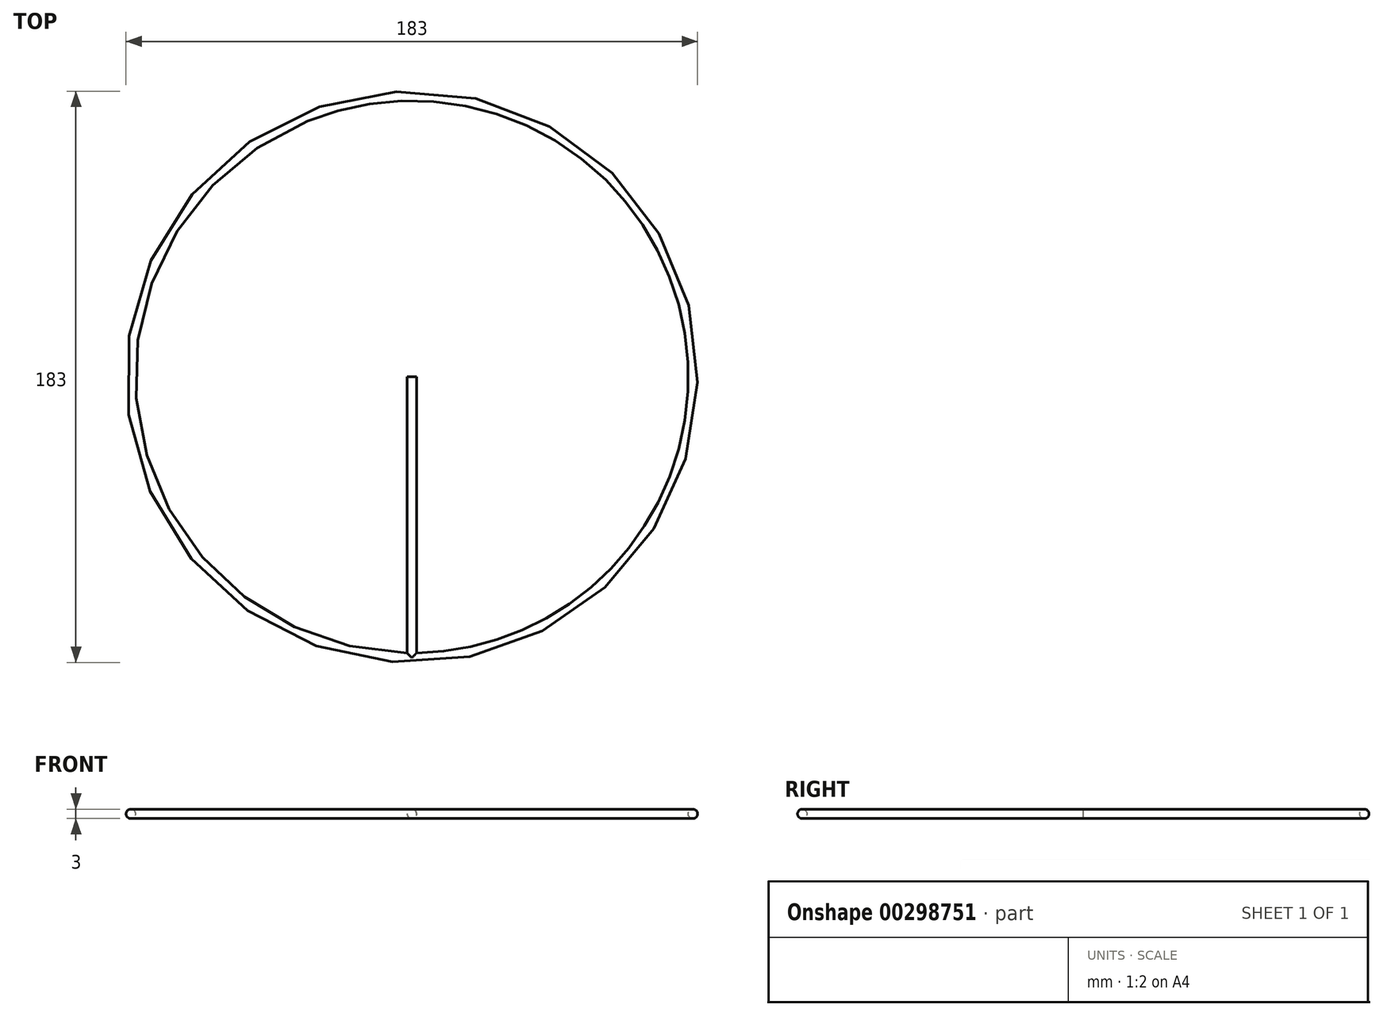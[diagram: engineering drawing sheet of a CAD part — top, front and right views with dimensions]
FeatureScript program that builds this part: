
annotation { "Feature Type Name" : "Feature", "Feature Type Description" : "" }
export const myFeature = defineFeature(function(context is Context, id is Id, definition is map)
    precondition{}
    {
        {
            var Q0;
            Q0=qCreatedBy(makeId("Top.planeOp"),FACE);
            var sketch = newSketch(context, id + "F0", { "sketchPlane" : qUnion([Q0])});
            skCircle(sketch, "E0", {"center": v(0, 0) * mm, "radius": 90 * mm});
            skLineSegment(sketch, "E1", {"start": v(0, 90) * mm, "end": v(0, 0) * mm});
            skLineSegment(sketch, "E2", {"start": v(0, 0) * mm, "end": v(-77.94, -45) * mm});
            skLineSegment(sketch, "E3", {"start": v(0, 0) * mm, "end": v(77.94, -45) * mm});
            skSolve(sketch);
        }
        {
            var Q0;
            Q0=qCreatedBy(makeId("Front.planeOp"),FACE);
            var sketch = newSketch(context, id + "F1", { "sketchPlane" : qUnion([Q0])});
            skCircle(sketch, "E4", {"center": v(0, 0) * mm, "radius": 1.5 * mm});
            skCircle(sketch, "E5", {"center": v(-90, 0) * mm, "radius": 1.5 * mm});
            skSolve(sketch);
        }
        {
            var Q0;
            Q0=makeQuery(id+"F1.imprint","IMPRINT",FACE,{"disambiguationData":[TD([[makeQuery(id+"F1.imprint","IMPRINT",EDGE,{"derivedFrom":sQuery(id+"F1.wireOp",EDGE,"E5")}),1.0]])]});
            var Q1;
            Q1=sQuery(id+"F0.wireOp",EDGE,"E0");
            revolve(context, id + "F2", {"entities" : qUnion([Q0]), "axis" : qUnion([Q1]), "revolveType" : RevolveType.FULL});
        }
        {
            var Q0;
            Q0=qCreatedBy(makeId("Front.planeOp"),FACE);
            var sketch = newSketch(context, id + "F3", { "sketchPlane" : qUnion([Q0])});
            skCircle(sketch, "E6", {"center": v(0, 0) * mm, "radius": 1.5 * mm});
            skSolve(sketch);
        }
        {
            var Q0;
            Q0 = qSketchRegion(id + "F3", true);
            extrude(context, id + "F4", {"entities" : qUnion([Q0]), "operationType" : NewBodyOperationType.ADD, "depth" : 90 * mm});
        }
    });
